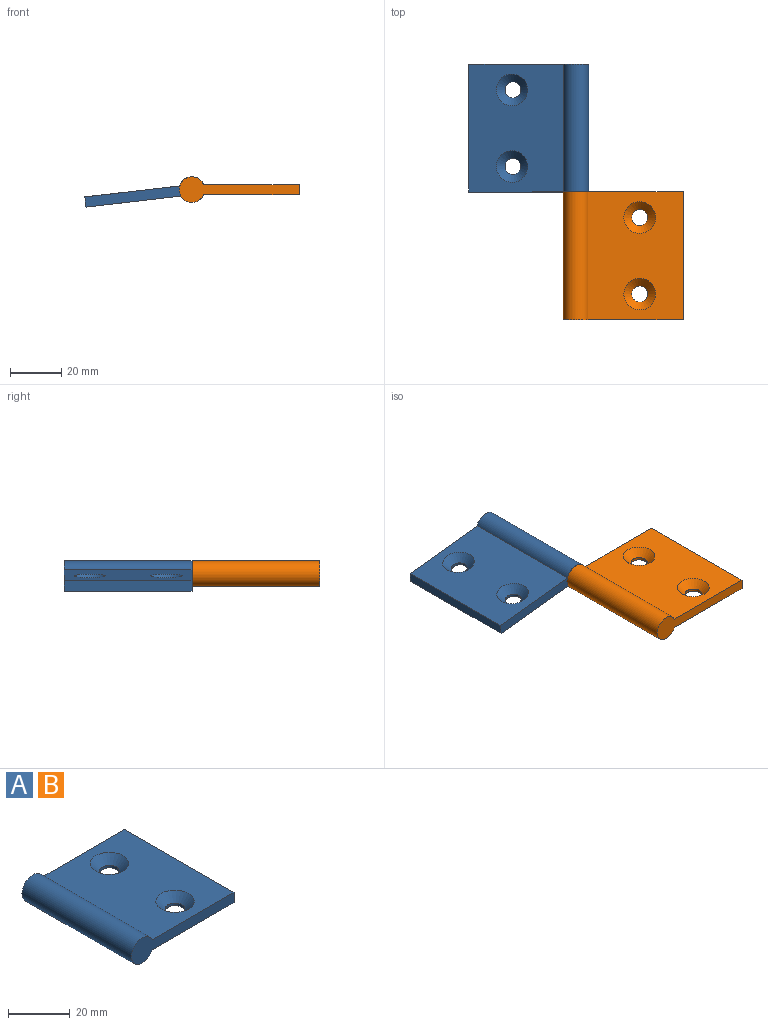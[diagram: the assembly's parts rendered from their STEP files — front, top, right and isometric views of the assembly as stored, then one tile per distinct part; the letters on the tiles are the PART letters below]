
ASSEMBLY  parts=2 mates=1
PART A: 10 faces, bbox 47x50x10 mm
  f0: plane 50x37.42mm, normal (0,0,1), area 1629.3mm2, adj f2,f3,f4,f5,f8,f9
  f1: plane 50x37.42mm, normal (0,0,-1), area 1806.5mm2, adj f2,f3,f4,f5,f6,f7
  f2: cylinder r=5mm len=50mm, axis (0,1,0), area 1365mm2, adj f0,f1,f4,f5
  f3: plane 50x4mm, normal (1,0,0), area 200mm2, adj f0,f1,f4,f5
  f4: plane 47x10mm, normal (0,-1,0), area 227.1mm2, adj f0,f1,f2,f3
  f5: plane 47x10mm, normal (0,1,0), area 227.1mm2, adj f0,f1,f2,f3
  f6: cylinder r=3.2mm len=6.4mm, axis (0,0,1), area 20.1mm2, adj f1,f9
  f7: cylinder r=3.2mm len=6.4mm, axis (0,0,1), area 20.1mm2, adj f1,f8
  f8: cone r=3.2mm half-angle=45deg, axis (0,0,1), area 125.3mm2, adj f0,f7
  f9: cone r=6.2mm half-angle=45deg, axis (0,0,1), area 125.3mm2, adj f0,f6
PART B: same geometry as A
PLACE A rot(axis=(0.06,0,-1),180deg) t=(-24.84,-7.81,-31.6)mm
PLACE B t=(-24.84,-7.81,-31.6)mm fixed
MATE revolute B.f2 <-> A.f2  axis (0,1,0) through (-24.84,-7.81,-31.6)mm
